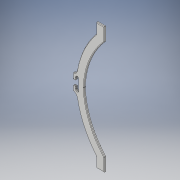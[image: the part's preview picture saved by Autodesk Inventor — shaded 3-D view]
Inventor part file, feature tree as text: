
AUTODESK INVENTOR PART (.ipt)
format: ipt  version: 2018 (Build 220112000, 112)  size: 625,152 bytes
history: native  units: mm
features: extrude x3, sketch x3, fillet x2, mirror x1
ambient origin geometry x8: Origin, YZ Plane, XZ Plane, XY Plane, X Axis, Y Axis, Z Axis, Center Point
bodies: Volumenkörper1 (feature_tree)
feature tree (9):
  extrude  "Extrusion1"  Depth=15.0mm
  mirror  "Spiegeln1"
  extrude  "Extrusion2"  TaperAngle=0.0deg  [1 undecoded]
  fillet  "Rundung1"  Radius=120.0mm
  fillet  "Rundung2"  Radius=150.0mm
  extrude  "Extrusion3"  Depth=15.0mm
  sketch  "Skizze1"  dims[d0=25.0mm d2=15.0mm]
  sketch  "Skizze2"  dims[d4=54.0mm d5=0.0mm d6=120.0mm d7=150.0mm]
  sketch  "Skizze3"  dims[d9=5.0mm d10=15.0mm d11=15.0mm d12=4.0mm d13=0.0mm d15=10.0mm d16=5.0mm d17=10.0mm d18=5.0mm d19=5.0mm d20=24.0mm d21=4.5mm d22=4.0mm d23=0.0mm d24=10.0mm d25=1.0mm d26=1.0mm d27=0.0mm]
note: 1 required parameter value undecoded (feature->parameter linkage not recoverable at this tier; creation-order binding heuristic only, values carry confidence <= 0.55)
